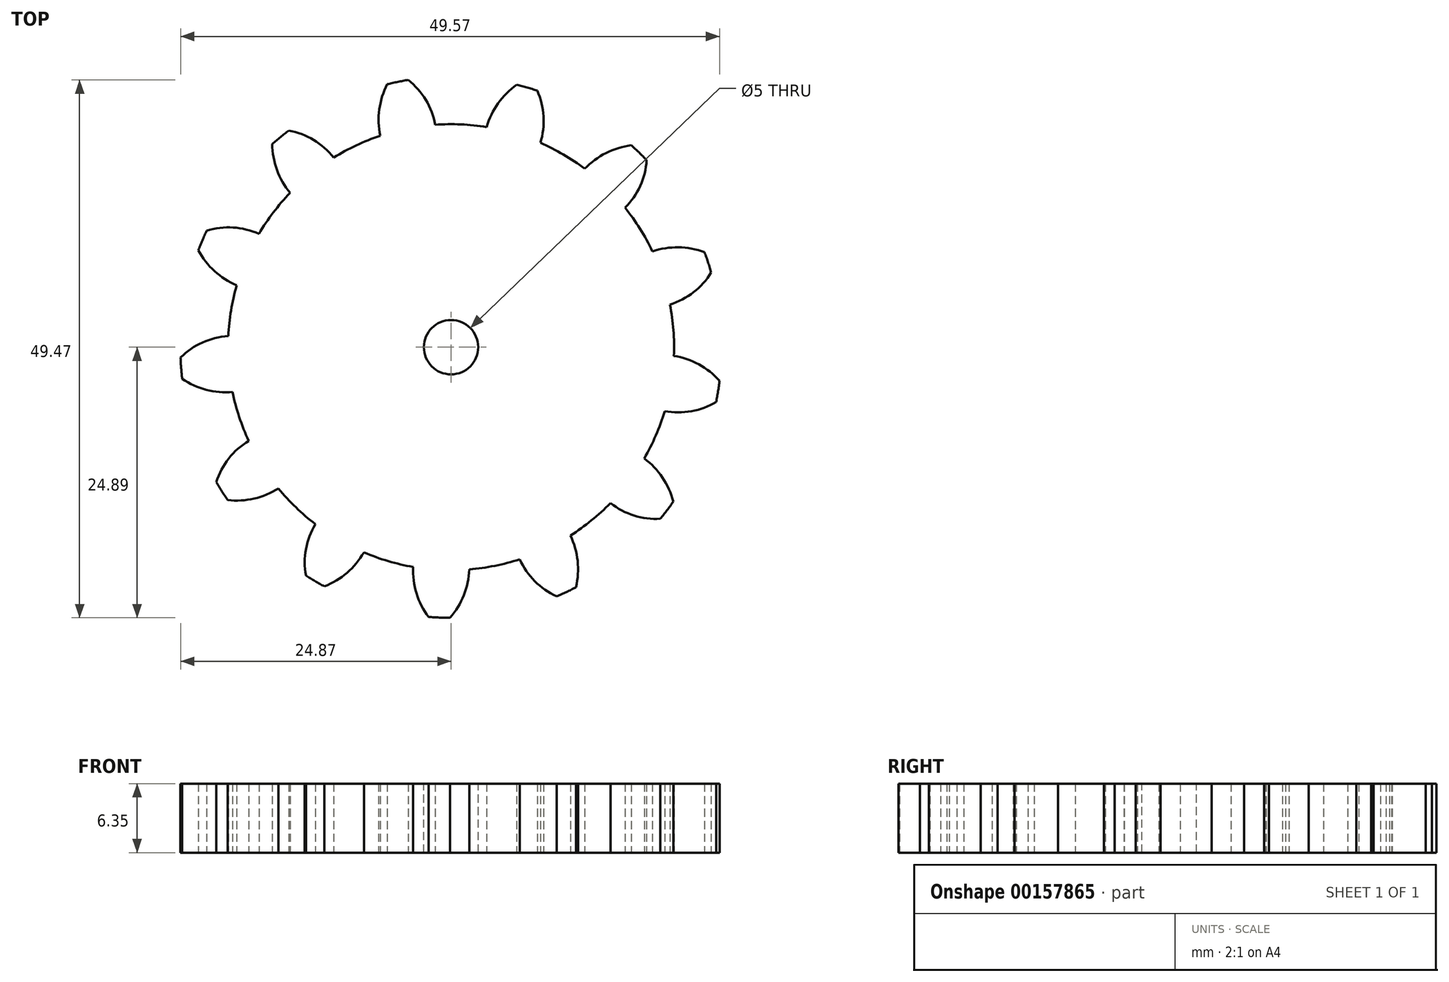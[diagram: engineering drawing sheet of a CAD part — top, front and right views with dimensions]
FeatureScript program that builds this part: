
annotation { "Feature Type Name" : "Feature", "Feature Type Description" : "" }
export const myFeature = defineFeature(function(context is Context, id is Id, definition is map)
    precondition{}
    {
        {
            var Q0;
            Q0=qCreatedBy(makeId("Top.planeOp"),FACE);
            var sketch = newSketch(context, id + "F0", { "sketchPlane" : qUnion([Q0])});
            skCircle(sketch, "E0", {"center": v(0, 0) * mm, "radius": 25.4 * mm, "construction": true});
            skCircle(sketch, "E1", {"center": v(0, 0) * mm, "radius": 24.9 * mm});
            skCircle(sketch, "E2", {"center": v(0, 0) * mm, "radius": 22.13 * mm, "construction": true});
            skCircle(sketch, "E3", {"center": v(0, 0) * mm, "radius": 20.9 * mm, "construction": true});
            skLineSegment(sketch, "E4", {"start": v(0, 20.9) * mm, "end": v(0, 25.4) * mm, "construction": true});
            skLineSegment(sketch, "E5", {"start": v(-6.36, 24.6) * mm, "end": v(-5.23, 20.23) * mm, "construction": true});
            skLineSegment(sketch, "E6", {"start": v(-5.23, 20.23) * mm, "end": v(0, 22.13) * mm, "construction": true});
            skLineSegment(sketch, "E7", {"start": v(-13.83, 20.7) * mm, "end": v(-14.11, 21.12) * mm});
            skLineSegment(sketch, "E8", {"start": v(0, 22.13) * mm, "end": v(6.63, 24.52) * mm, "construction": true});
            skLineSegment(sketch, "E9", {"start": v(10.24, 18.22) * mm, "end": v(3.9, 21.78) * mm, "construction": true});
            skCircle(sketch, "E10", {"center": v(10.24, 18.22) * mm, "radius": 7.26 * mm});
            skLineSegment(sketch, "E11", {"start": v(3.9, 21.78) * mm, "end": v(4.4, 24.5) * mm, "construction": true});
            skLineSegment(sketch, "E12", {"start": v(15.28, 19.65) * mm, "end": v(13.58, 17.47) * mm, "construction": true});
            skLineSegment(sketch, "E13", {"start": v(10.13, 22.74) * mm, "end": v(9, 20.21) * mm, "construction": true});
            skLineSegment(sketch, "E14", {"start": v(3.9, 21.78) * mm, "end": v(10.13, 22.74) * mm, "construction": true});
            skLineSegment(sketch, "E15", {"start": v(13.58, 17.47) * mm, "end": v(10.13, 22.74) * mm, "construction": true});
            skCircle(sketch, "E16", {"center": v(0, 0) * mm, "radius": 20.5 * mm});
            skLineSegment(sketch, "E17", {"start": v(5.68, 19.55) * mm, "end": v(3.26, 20.25) * mm, "construction": true});
            skLineSegment(sketch, "E18", {"start": v(9, 20.21) * mm, "end": v(8.5, 20.25) * mm});
            skLineSegment(sketch, "E19", {"start": v(8.5, 20.25) * mm, "end": v(1.77, 20.83) * mm, "construction": true});
            skCircle(sketch, "E20", {"center": v(1.77, 20.83) * mm, "radius": 6.75 * mm});
            skLineSegment(sketch, "E21", {"start": v(5.68, 19.55) * mm, "end": v(7.21, 24.82) * mm, "construction": true});
            skLineSegment(sketch, "E22", {"start": v(9, 20.21) * mm, "end": v(3.9, 21.78) * mm, "construction": true});
            skSolve(sketch);
        }
        {
            var Q0;
            {var subQ0=sQuery(id+"F0.wireOp",EDGE,"E20");var subQ3=sQuery(id+"F0.wireOp",EDGE,"E10");var subQ4=makeQuery(id+"F0.imprint","INTERSECT",VERTEX,{"disambiguationData":[OD(1.0)],"derivedFrom":[subQ3,subQ0]});Q0=makeQuery(id+"F0.imprint","IMPRINT",FACE,{"disambiguationData":[TD([[makeQuery(id+"F0.imprint","IMPRINT",EDGE,{"disambiguationData":[TD([[subQ4,-1.0]])],"derivedFrom":subQ3}),-1.0]])]});}
            var Q1;
            {var subQ0=sQuery(id+"F0.wireOp",EDGE,"E20");var subQ3=sQuery(id+"F0.wireOp",EDGE,"E10");var subQ4=makeQuery(id+"F0.imprint","INTERSECT",VERTEX,{"disambiguationData":[OD(1.0)],"derivedFrom":[subQ3,subQ0]});Q1=makeQuery(id+"F0.imprint","IMPRINT",FACE,{"disambiguationData":[TD([[makeQuery(id+"F0.imprint","IMPRINT",EDGE,{"disambiguationData":[TD([[subQ4,-1.0]])],"derivedFrom":subQ3}),1.0]])]});}
            var Q2;
            {var subQ1=sQuery(id+"F0.wireOp",EDGE,"E16");var subQ3=sQuery(id+"F0.wireOp",EDGE,"E10");var subQ5=makeQuery(id+"F0.imprint","INTERSECT",VERTEX,{"disambiguationData":[OD(0.0)],"derivedFrom":[subQ3,subQ1]});Q2=makeQuery(id+"F0.imprint","IMPRINT",FACE,{"disambiguationData":[TD([[makeQuery(id+"F0.imprint","IMPRINT",EDGE,{"disambiguationData":[TD([[subQ5,-1.0]])],"derivedFrom":subQ3}),1.0]])]});}
            var Q3;
            {var subQ1=sQuery(id+"F0.wireOp",EDGE,"E16");var subQ3=sQuery(id+"F0.wireOp",EDGE,"E10");var subQ5=makeQuery(id+"F0.imprint","INTERSECT",VERTEX,{"disambiguationData":[OD(0.0)],"derivedFrom":[subQ3,subQ1]});Q3=makeQuery(id+"F0.imprint","IMPRINT",FACE,{"disambiguationData":[TD([[makeQuery(id+"F0.imprint","IMPRINT",EDGE,{"disambiguationData":[TD([[subQ5,-1.0]])],"derivedFrom":subQ3}),-1.0]])]});}
            var Q4;
            {var subQ0=sQuery(id+"F0.wireOp",EDGE,"E20");var subQ3=makeQuery(id+"F0.imprint","IMPRINT",VERTEX,{"derivedFrom":subQ0});Q4=makeQuery(id+"F0.imprint","IMPRINT",FACE,{"disambiguationData":[TD([[makeQuery(id+"F0.imprint","IMPRINT",EDGE,{"disambiguationData":[TD([[subQ3,-1.0]])],"derivedFrom":subQ0}),1.0]])]});}
            extrude(context, id + "F1", {"entities" : qUnion([Q0, Q1, Q2, Q3, Q4]), "depth" : 6.35 * mm});
        }
        {
            var Q0;
            Q0=makeQuery(id+"F1.opExtrude","SWEPT_BODY",BODY,{"disambiguationData":[OSD([sQuery(id+"F0.wireOp",EDGE,"E1"),sQuery(id+"F0.wireOp",EDGE,"E10"),sQuery(id+"F0.wireOp",EDGE,"E16"),sQuery(id+"F0.wireOp",EDGE,"E20")])]});
            var Q1;
            Q1=makeQuery(id+"F1.opExtrude","CAP_EDGE",EDGE,{"disambiguationData":[OSD([sQuery(id+"F0.wireOp",EDGE,"E16")])],"isStart":false});
            circularPattern(context, id + "F2", {"operationType" : NewBodyOperationType.ADD, "entities" : qUnion([Q0]), "axis" : qUnion([Q1]), "angle" : 360 * degree, "instanceCount" : 13, "equalSpace" : true});
        }
        {
            var Q0;
            {var subQ0=makeQuery(id+"F1.opExtrude","CAP_FACE",FACE,{"disambiguationData":[OSD([sQuery(id+"F0.wireOp",EDGE,"E1"),sQuery(id+"F0.wireOp",EDGE,"E10"),sQuery(id+"F0.wireOp",EDGE,"E16"),sQuery(id+"F0.wireOp",EDGE,"E20")])],"isStart":false});Q0=makeQuery(id+"F2.boolean.opBoolean","MERGE",FACE,{"derivedFrom":[subQ0,makeQuery(id+"F2.opPattern","COPY",FACE,{"derivedFrom":subQ0,"instanceName":"1"}),makeQuery(id+"F2.opPattern","COPY",FACE,{"derivedFrom":subQ0,"instanceName":"2"}),makeQuery(id+"F2.opPattern","COPY",FACE,{"derivedFrom":subQ0,"instanceName":"3"}),makeQuery(id+"F2.opPattern","COPY",FACE,{"derivedFrom":subQ0,"instanceName":"4"}),makeQuery(id+"F2.opPattern","COPY",FACE,{"derivedFrom":subQ0,"instanceName":"5"}),makeQuery(id+"F2.opPattern","COPY",FACE,{"derivedFrom":subQ0,"instanceName":"6"}),makeQuery(id+"F2.opPattern","COPY",FACE,{"derivedFrom":subQ0,"instanceName":"7"}),makeQuery(id+"F2.opPattern","COPY",FACE,{"derivedFrom":subQ0,"instanceName":"8"}),makeQuery(id+"F2.opPattern","COPY",FACE,{"derivedFrom":subQ0,"instanceName":"9"}),makeQuery(id+"F2.opPattern","COPY",FACE,{"derivedFrom":subQ0,"instanceName":"10"}),makeQuery(id+"F2.opPattern","COPY",FACE,{"derivedFrom":subQ0,"instanceName":"11"}),makeQuery(id+"F2.opPattern","COPY",FACE,{"derivedFrom":subQ0,"instanceName":"12"})]});}
            var sketch = newSketch(context, id + "F3", { "sketchPlane" : qUnion([Q0])});
            skCircle(sketch, "E23", {"center": v(0, 0) * mm, "radius": 2.5 * mm});
            skSolve(sketch);
        }
        {
            var Q0;
            Q0 = qSketchRegion(id + "F3", true);
            extrude(context, id + "F4", {"entities" : qUnion([Q0]), "operationType" : NewBodyOperationType.REMOVE, "endBound" : BoundingType.THROUGH_ALL, "oppositeDirection" : true, "depth" : 25.4 * mm});
        }
    });
